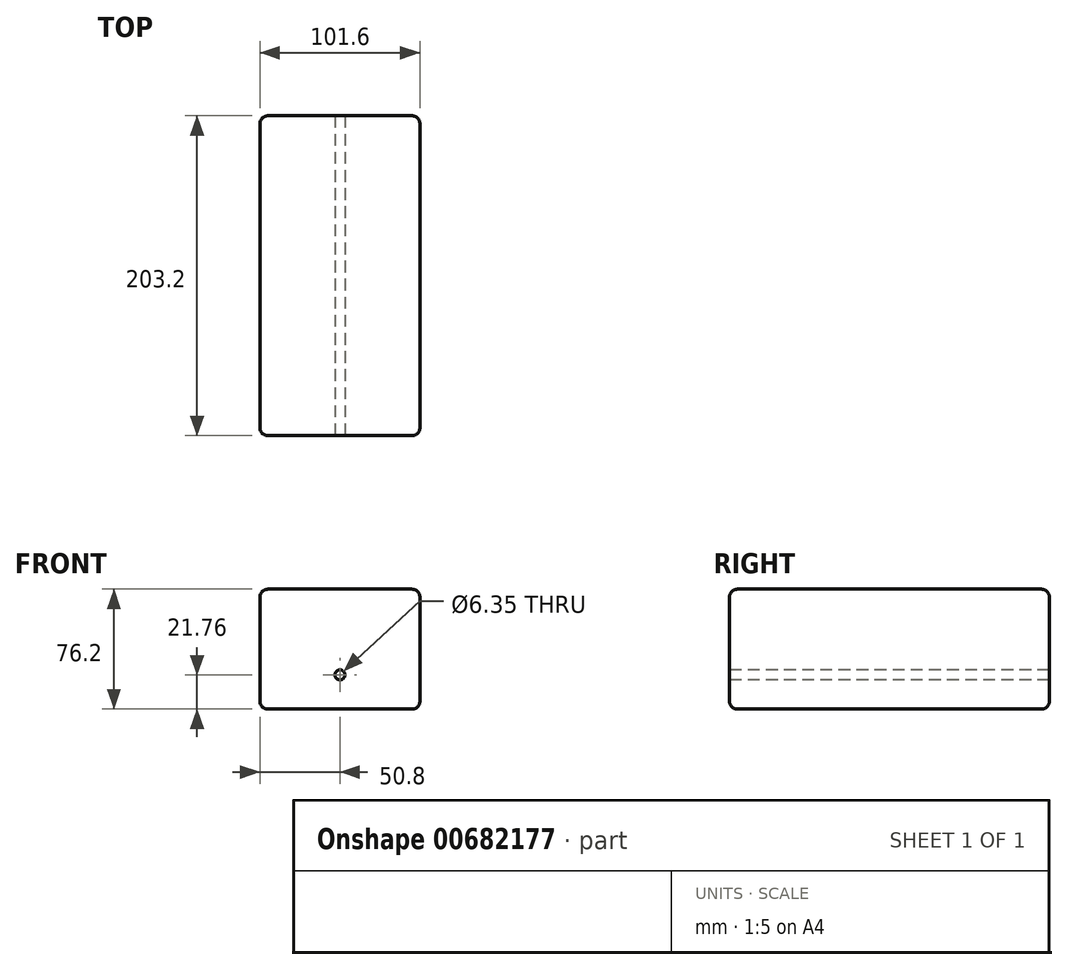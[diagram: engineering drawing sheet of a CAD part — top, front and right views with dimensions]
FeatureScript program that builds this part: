
annotation { "Feature Type Name" : "Feature", "Feature Type Description" : "" }
export const myFeature = defineFeature(function(context is Context, id is Id, definition is map)
    precondition{}
    {
        {
            var Q0;
            Q0=qCreatedBy(makeId("Front.planeOp"),FACE);
            var sketch = newSketch(context, id + "F0", { "sketchPlane" : qUnion([Q0])});
            skLineSegment(sketch, "E0.bottom", {"start": v(-50.8, -38.1) * mm, "end": v(50.8, -38.1) * mm});
            skLineSegment(sketch, "E0.top", {"start": v(-50.8, 38.1) * mm, "end": v(50.8, 38.1) * mm});
            skLineSegment(sketch, "E0.left", {"start": v(-50.8, -38.1) * mm, "end": v(-50.8, 38.1) * mm});
            skLineSegment(sketch, "E0.right", {"start": v(50.8, -38.1) * mm, "end": v(50.8, 38.1) * mm});
            skPoint(sketch, "E0.middle", {"position": v(0, 0) * mm});
            skSolve(sketch);
        }
        {
            var Q0;
            Q0 = qSketchRegion(id + "F0", true);
            extrude(context, id + "F1", {"entities" : qUnion([Q0]), "endBound" : BoundingType.SYMMETRIC, "depth" : 203.2 * mm, "offsetDistance" : 25.4 * mm});
        }
        {
            var Q0;
            Q0=makeQuery(id+"F1.opExtrude","CAP_EDGE",EDGE,{"disambiguationData":[OSD([sQuery(id+"F0.wireOp",EDGE,"E0.top")])],"isStart":false});
            var Q1;
            Q1=makeQuery(id+"F1.opExtrude","SWEPT_EDGE",EDGE,{"disambiguationData":[OSD([sQuery(id+"F0.wireOp",EDGE,"E0.top"),sQuery(id+"F0.wireOp",EDGE,"E0.right")])]});
            var Q2;
            Q2=makeQuery(id+"F1.opExtrude","SWEPT_EDGE",EDGE,{"disambiguationData":[OSD([sQuery(id+"F0.wireOp",EDGE,"E0.top"),sQuery(id+"F0.wireOp",EDGE,"E0.left")])]});
            var Q3;
            Q3=makeQuery(id+"F1.opExtrude","CAP_EDGE",EDGE,{"disambiguationData":[OSD([sQuery(id+"F0.wireOp",EDGE,"E0.left")])],"isStart":false});
            var Q4;
            Q4=makeQuery(id+"F1.opExtrude","CAP_EDGE",EDGE,{"disambiguationData":[OSD([sQuery(id+"F0.wireOp",EDGE,"E0.right")])],"isStart":false});
            var Q5;
            Q5=makeQuery(id+"F1.opExtrude","CAP_FACE",FACE,{"disambiguationData":[OSD([sQuery(id+"F0.wireOp",EDGE,"E0.bottom"),sQuery(id+"F0.wireOp",EDGE,"E0.top"),sQuery(id+"F0.wireOp",EDGE,"E0.left"),sQuery(id+"F0.wireOp",EDGE,"E0.right")])],"isStart":true});
            var Q6;
            Q6=makeQuery(id+"F1.opExtrude","SWEPT_FACE",FACE,{"disambiguationData":[OSD([sQuery(id+"F0.wireOp",EDGE,"E0.right")])]});
            var Q7;
            Q7=makeQuery(id+"F1.opExtrude","SWEPT_EDGE",EDGE,{"disambiguationData":[OSD([sQuery(id+"F0.wireOp",EDGE,"E0.bottom"),sQuery(id+"F0.wireOp",EDGE,"E0.right")])]});
            var Q8;
            Q8=makeQuery(id+"F1.opExtrude","SWEPT_EDGE",EDGE,{"disambiguationData":[OSD([sQuery(id+"F0.wireOp",EDGE,"E0.bottom"),sQuery(id+"F0.wireOp",EDGE,"E0.left")])]});
            fillet(context, id + "F2", {"entities" : qUnion([Q0, Q1, Q2, Q3, Q4, Q5, Q6, Q7, Q8]), "radius" : 5.08 * mm, "tangentPropagation" : true, "allowEdgeOverflow" : false});
        }
        {
            var Q0;
            Q0=makeQuery(id+"FGfTKkmkADLqAxq_1.opShell","OFFSET_EDGE",EDGE,{"disambiguationData":[OSD([sQuery(id+"F0.wireOp",EDGE,"E0.top"),sQuery(id+"F0.wireOp",EDGE,"E0.right")])]});
            var Q1;
            {var subQ0=sQuery(id+"F0.wireOp",EDGE,"E0.top");var subQ1=makeQuery(id+"F1.opExtrude","CAP_EDGE",EDGE,{"disambiguationData":[OSD([subQ0])],"isStart":true});var subQ2=sQuery(id+"F0.wireOp",EDGE,"E0.right");var subQ3=sQuery(id+"F0.wireOp",EDGE,"E0.left");var subQ4=sQuery(id+"F0.wireOp",EDGE,"E0.bottom");Q1=makeQuery(id+"FGfTKkmkADLqAxq_1.opShell","OFFSET_EDGE",EDGE,{"disambiguationData":[OSD([subQ4,subQ0,subQ3,subQ2]),TDD([makeQuery(id+"F2.opFillet","BLEND_EDGE",EDGE,{"blendedFrom":[subQ1,makeQuery(id+"F1.opExtrude","CAP_FACE",FACE,{"disambiguationData":[OSD([subQ4,subQ0,subQ3,subQ2])],"isStart":true})],"blendedInto":[makeQuery(id+"F1.opExtrude","CAP_FACE",FACE,{"disambiguationData":[OSD([subQ4,subQ0,subQ3,subQ2])],"isStart":true})]}),makeQuery(id+"F2.opFillet","BLEND_EDGE",EDGE,{"blendedFrom":[subQ1,makeQuery(id+"F1.opExtrude","SWEPT_FACE",FACE,{"disambiguationData":[OSD([subQ0])]})],"blendedInto":[makeQuery(id+"F1.opExtrude","SWEPT_FACE",FACE,{"disambiguationData":[OSD([subQ0])]})]})])]});}
            var Q2;
            {var subQ0=sQuery(id+"F0.wireOp",EDGE,"E0.left");var subQ1=makeQuery(id+"F1.opExtrude","CAP_EDGE",EDGE,{"disambiguationData":[OSD([subQ0])],"isStart":true});var subQ2=sQuery(id+"F0.wireOp",EDGE,"E0.right");var subQ3=sQuery(id+"F0.wireOp",EDGE,"E0.top");var subQ4=sQuery(id+"F0.wireOp",EDGE,"E0.bottom");Q2=makeQuery(id+"FGfTKkmkADLqAxq_1.opShell","OFFSET_EDGE",EDGE,{"disambiguationData":[OSD([subQ4,subQ3,subQ0,subQ2]),TDD([makeQuery(id+"F2.opFillet","BLEND_EDGE",EDGE,{"blendedFrom":[subQ1,makeQuery(id+"F1.opExtrude","CAP_FACE",FACE,{"disambiguationData":[OSD([subQ4,subQ3,subQ0,subQ2])],"isStart":true})],"blendedInto":[makeQuery(id+"F1.opExtrude","CAP_FACE",FACE,{"disambiguationData":[OSD([subQ4,subQ3,subQ0,subQ2])],"isStart":true})]}),makeQuery(id+"F2.opFillet","BLEND_EDGE",EDGE,{"blendedFrom":[subQ1,makeQuery(id+"F1.opExtrude","SWEPT_FACE",FACE,{"disambiguationData":[OSD([subQ0])]})],"blendedInto":[makeQuery(id+"F1.opExtrude","SWEPT_FACE",FACE,{"disambiguationData":[OSD([subQ0])]})]})])]});}
            var Q3;
            {var subQ0=sQuery(id+"F0.wireOp",EDGE,"E0.right");var subQ1=makeQuery(id+"F1.opExtrude","CAP_EDGE",EDGE,{"disambiguationData":[OSD([subQ0])],"isStart":true});var subQ2=sQuery(id+"F0.wireOp",EDGE,"E0.left");var subQ3=sQuery(id+"F0.wireOp",EDGE,"E0.top");var subQ4=sQuery(id+"F0.wireOp",EDGE,"E0.bottom");Q3=makeQuery(id+"FGfTKkmkADLqAxq_1.opShell","OFFSET_EDGE",EDGE,{"disambiguationData":[OSD([subQ4,subQ3,subQ2,subQ0]),TDD([makeQuery(id+"F2.opFillet","BLEND_EDGE",EDGE,{"blendedFrom":[subQ1,makeQuery(id+"F1.opExtrude","CAP_FACE",FACE,{"disambiguationData":[OSD([subQ4,subQ3,subQ2,subQ0])],"isStart":true})],"blendedInto":[makeQuery(id+"F1.opExtrude","CAP_FACE",FACE,{"disambiguationData":[OSD([subQ4,subQ3,subQ2,subQ0])],"isStart":true})]}),makeQuery(id+"F2.opFillet","BLEND_EDGE",EDGE,{"blendedFrom":[subQ1,makeQuery(id+"F1.opExtrude","SWEPT_FACE",FACE,{"disambiguationData":[OSD([subQ0])]})],"blendedInto":[makeQuery(id+"F1.opExtrude","SWEPT_FACE",FACE,{"disambiguationData":[OSD([subQ0])]})]})])]});}
            var Q4;
            Q4=makeQuery(id+"FGfTKkmkADLqAxq_1.opShell","OFFSET_EDGE",EDGE,{"disambiguationData":[OSD([sQuery(id+"F0.wireOp",EDGE,"E0.top"),sQuery(id+"F0.wireOp",EDGE,"E0.left")])]});
            var Q5;
            {var subQ0=sQuery(id+"F0.wireOp",EDGE,"E0.right");var subQ1=sQuery(id+"F0.wireOp",EDGE,"E0.left");var subQ2=sQuery(id+"F0.wireOp",EDGE,"E0.top");var subQ3=sQuery(id+"F0.wireOp",EDGE,"E0.bottom");var subQ4=makeQuery(id+"F1.opExtrude","CAP_EDGE",EDGE,{"disambiguationData":[OSD([subQ3])],"isStart":true});Q5=makeQuery(id+"FGfTKkmkADLqAxq_1.opShell","OFFSET_EDGE",EDGE,{"disambiguationData":[OSD([subQ3,subQ2,subQ1,subQ0]),TDD([makeQuery(id+"F2.opFillet","BLEND_EDGE",EDGE,{"blendedFrom":[subQ4,makeQuery(id+"F1.opExtrude","SWEPT_FACE",FACE,{"disambiguationData":[OSD([subQ3])]})],"blendedInto":[makeQuery(id+"F1.opExtrude","SWEPT_FACE",FACE,{"disambiguationData":[OSD([subQ3])]})]}),makeQuery(id+"F2.opFillet","BLEND_EDGE",EDGE,{"blendedFrom":[subQ4,makeQuery(id+"F1.opExtrude","CAP_FACE",FACE,{"disambiguationData":[OSD([subQ3,subQ2,subQ1,subQ0])],"isStart":true})],"blendedInto":[makeQuery(id+"F1.opExtrude","CAP_FACE",FACE,{"disambiguationData":[OSD([subQ3,subQ2,subQ1,subQ0])],"isStart":true})]})])]});}
            var Q6;
            Q6=makeQuery(id+"FGfTKkmkADLqAxq_1.opShell","OFFSET_EDGE",EDGE,{"disambiguationData":[OSD([sQuery(id+"F0.wireOp",EDGE,"E0.bottom"),sQuery(id+"F0.wireOp",EDGE,"E0.left")])]});
            var Q7;
            Q7=makeQuery(id+"FGfTKkmkADLqAxq_1.opShell","OFFSET_EDGE",EDGE,{"disambiguationData":[OSD([sQuery(id+"F0.wireOp",EDGE,"E0.bottom")])]});
            var Q8;
            {var subQ0=sQuery(id+"F0.wireOp",EDGE,"E0.left");var subQ1=makeQuery(id+"F1.opExtrude","CAP_EDGE",EDGE,{"disambiguationData":[OSD([subQ0])],"isStart":false});var subQ2=sQuery(id+"F0.wireOp",EDGE,"E0.right");var subQ3=sQuery(id+"F0.wireOp",EDGE,"E0.top");var subQ4=sQuery(id+"F0.wireOp",EDGE,"E0.bottom");Q8=makeQuery(id+"FGfTKkmkADLqAxq_1.opShell","OFFSET_EDGE",EDGE,{"disambiguationData":[OSD([subQ4,subQ3,subQ0,subQ2]),TDD([makeQuery(id+"F2.opFillet","BLEND_EDGE",EDGE,{"blendedFrom":[subQ1,makeQuery(id+"F1.opExtrude","CAP_FACE",FACE,{"disambiguationData":[OSD([subQ4,subQ3,subQ0,subQ2])],"isStart":false})],"blendedInto":[makeQuery(id+"F1.opExtrude","CAP_FACE",FACE,{"disambiguationData":[OSD([subQ4,subQ3,subQ0,subQ2])],"isStart":false})]}),makeQuery(id+"F2.opFillet","BLEND_EDGE",EDGE,{"blendedFrom":[subQ1,makeQuery(id+"F1.opExtrude","SWEPT_FACE",FACE,{"disambiguationData":[OSD([subQ0])]})],"blendedInto":[makeQuery(id+"F1.opExtrude","SWEPT_FACE",FACE,{"disambiguationData":[OSD([subQ0])]})]})])]});}
            var Q9;
            {var subQ0=sQuery(id+"F0.wireOp",EDGE,"E0.top");var subQ1=makeQuery(id+"F1.opExtrude","CAP_EDGE",EDGE,{"disambiguationData":[OSD([subQ0])],"isStart":false});var subQ2=sQuery(id+"F0.wireOp",EDGE,"E0.right");var subQ3=sQuery(id+"F0.wireOp",EDGE,"E0.left");var subQ4=sQuery(id+"F0.wireOp",EDGE,"E0.bottom");Q9=makeQuery(id+"FGfTKkmkADLqAxq_1.opShell","OFFSET_EDGE",EDGE,{"disambiguationData":[OSD([subQ4,subQ0,subQ3,subQ2]),TDD([makeQuery(id+"F2.opFillet","BLEND_EDGE",EDGE,{"blendedFrom":[subQ1,makeQuery(id+"F1.opExtrude","CAP_FACE",FACE,{"disambiguationData":[OSD([subQ4,subQ0,subQ3,subQ2])],"isStart":false})],"blendedInto":[makeQuery(id+"F1.opExtrude","CAP_FACE",FACE,{"disambiguationData":[OSD([subQ4,subQ0,subQ3,subQ2])],"isStart":false})]}),makeQuery(id+"F2.opFillet","BLEND_EDGE",EDGE,{"blendedFrom":[subQ1,makeQuery(id+"F1.opExtrude","SWEPT_FACE",FACE,{"disambiguationData":[OSD([subQ0])]})],"blendedInto":[makeQuery(id+"F1.opExtrude","SWEPT_FACE",FACE,{"disambiguationData":[OSD([subQ0])]})]})])]});}
            var Q10;
            Q10=makeQuery(id+"FGfTKkmkADLqAxq_1.opShell","OFFSET_EDGE",EDGE,{"disambiguationData":[OSD([sQuery(id+"F0.wireOp",EDGE,"E0.bottom"),sQuery(id+"F0.wireOp",EDGE,"E0.right")])]});
            var Q11;
            {var subQ0=sQuery(id+"F0.wireOp",EDGE,"E0.right");var subQ1=makeQuery(id+"F1.opExtrude","CAP_EDGE",EDGE,{"disambiguationData":[OSD([subQ0])],"isStart":false});var subQ2=sQuery(id+"F0.wireOp",EDGE,"E0.left");var subQ3=sQuery(id+"F0.wireOp",EDGE,"E0.top");var subQ4=sQuery(id+"F0.wireOp",EDGE,"E0.bottom");Q11=makeQuery(id+"FGfTKkmkADLqAxq_1.opShell","OFFSET_EDGE",EDGE,{"disambiguationData":[OSD([subQ4,subQ3,subQ2,subQ0]),TDD([makeQuery(id+"F2.opFillet","BLEND_EDGE",EDGE,{"blendedFrom":[subQ1,makeQuery(id+"F1.opExtrude","CAP_FACE",FACE,{"disambiguationData":[OSD([subQ4,subQ3,subQ2,subQ0])],"isStart":false})],"blendedInto":[makeQuery(id+"F1.opExtrude","CAP_FACE",FACE,{"disambiguationData":[OSD([subQ4,subQ3,subQ2,subQ0])],"isStart":false})]}),makeQuery(id+"F2.opFillet","BLEND_EDGE",EDGE,{"blendedFrom":[subQ1,makeQuery(id+"F1.opExtrude","SWEPT_FACE",FACE,{"disambiguationData":[OSD([subQ0])]})],"blendedInto":[makeQuery(id+"F1.opExtrude","SWEPT_FACE",FACE,{"disambiguationData":[OSD([subQ0])]})]})])]});}
            var Q12;
            {var subQ0=sQuery(id+"F0.wireOp",EDGE,"E0.right");Q12=makeQuery(id+"F2.opFillet","BLEND_EDGE",EDGE,{"blendedFrom":[makeQuery(id+"F1.opExtrude","CAP_EDGE",EDGE,{"disambiguationData":[OSD([subQ0])],"isStart":false}),makeQuery(id+"F1.opExtrude","CAP_FACE",FACE,{"disambiguationData":[OSD([sQuery(id+"F0.wireOp",EDGE,"E0.bottom"),sQuery(id+"F0.wireOp",EDGE,"E0.top"),sQuery(id+"F0.wireOp",EDGE,"E0.left"),subQ0])],"isStart":false})],"blendedInto":[makeQuery(id+"F1.opExtrude","CAP_FACE",FACE,{"disambiguationData":[OSD([sQuery(id+"F0.wireOp",EDGE,"E0.bottom"),sQuery(id+"F0.wireOp",EDGE,"E0.top"),sQuery(id+"F0.wireOp",EDGE,"E0.left"),subQ0])],"isStart":false})]});}
            var Q13;
            {var subQ0=sQuery(id+"F0.wireOp",EDGE,"E0.bottom");Q13=makeQuery(id+"F2.opFillet","BLEND_EDGE",EDGE,{"blendedFrom":[makeQuery(id+"F1.opExtrude","SWEPT_EDGE",EDGE,{"disambiguationData":[OSD([subQ0,sQuery(id+"F0.wireOp",EDGE,"E0.right")])]}),makeQuery(id+"F1.opExtrude","SWEPT_FACE",FACE,{"disambiguationData":[OSD([subQ0])]})],"blendedInto":[makeQuery(id+"F1.opExtrude","SWEPT_FACE",FACE,{"disambiguationData":[OSD([subQ0])]})]});}
            var Q14;
            Q14=makeQuery(id+"F1.opExtrude","CAP_EDGE",EDGE,{"disambiguationData":[OSD([sQuery(id+"F0.wireOp",EDGE,"E0.bottom")])],"isStart":false});
            fillet(context, id + "F3", {"entities" : qUnion([Q0, Q1, Q2, Q3, Q4, Q5, Q6, Q7, Q8, Q9, Q10, Q11, Q12, Q13, Q14]), "radius" : 5.08 * mm, "tangentPropagation" : true, "allowEdgeOverflow" : false});
        }
        {
            var Q0;
            Q0=makeQuery(id+"F1.opExtrude","CAP_FACE",FACE,{"disambiguationData":[OSD([sQuery(id+"F0.wireOp",EDGE,"E0.bottom"),sQuery(id+"F0.wireOp",EDGE,"E0.top"),sQuery(id+"F0.wireOp",EDGE,"E0.left"),sQuery(id+"F0.wireOp",EDGE,"E0.right")])],"isStart":false});
            var sketch = newSketch(context, id + "F4", { "sketchPlane" : qUnion([Q0])});
            skCircle(sketch, "E1", {"center": v(0, -16.34) * mm, "radius": 3.18 * mm});
            skSolve(sketch);
        }
        {
            var Q0;
            Q0=makeQuery(id+"F4.imprint","IMPRINT",FACE,{"disambiguationData":[TD([[makeQuery(id+"F4.imprint","IMPRINT",EDGE,{"derivedFrom":sQuery(id+"F4.wireOp",EDGE,"E1")}),1.0]])]});
            var Q1;
            Q1=makeQuery(id+"F1.opExtrude","CAP_FACE",FACE,{"disambiguationData":[OSD([sQuery(id+"F0.wireOp",EDGE,"E0.bottom"),sQuery(id+"F0.wireOp",EDGE,"E0.top"),sQuery(id+"F0.wireOp",EDGE,"E0.left"),sQuery(id+"F0.wireOp",EDGE,"E0.right")])],"isStart":true});
            extrude(context, id + "F5", {"entities" : qUnion([Q0]), "operationType" : NewBodyOperationType.REMOVE, "endBound" : BoundingType.UP_TO_SURFACE, "oppositeDirection" : true, "depth" : 63.5 * mm, "endBoundEntityFace" : qUnion([Q1]), "offsetDistance" : 25.4 * mm});
        }
        {
            var Q0;
            Q0=makeQuery(id+"F1.opExtrude","CAP_FACE",FACE,{"disambiguationData":[OSD([sQuery(id+"F0.wireOp",EDGE,"E0.bottom"),sQuery(id+"F0.wireOp",EDGE,"E0.top"),sQuery(id+"F0.wireOp",EDGE,"E0.left"),sQuery(id+"F0.wireOp",EDGE,"E0.right")])],"isStart":false});
            var sketch = newSketch(context, id + "F6", { "sketchPlane" : qUnion([Q0])});
            skCircle(sketch, "E2", {"center": v(0, -16.34) * mm, "radius": 3.17 * mm});
            skSolve(sketch);
        }
        {
            var Q0;
            Q0 = qSketchRegion(id + "F6", true);
            var Q1;
            Q1=sQuery(id+"F6.wireOp",EDGE,"E2");
            extrude(context, id + "F7", {"entities" : qUnion([Q0]), "bodyType" : ToolBodyType.SURFACE, "surfaceEntities" : qUnion([Q1]), "depth" : 127 * mm, "offsetDistance" : 25.4 * mm});
        }
        {
            var Q0;
            Q0=makeQuery(id+"F1.opExtrude","CAP_FACE",FACE,{"disambiguationData":[OSD([sQuery(id+"F0.wireOp",EDGE,"E0.bottom"),sQuery(id+"F0.wireOp",EDGE,"E0.top"),sQuery(id+"F0.wireOp",EDGE,"E0.left"),sQuery(id+"F0.wireOp",EDGE,"E0.right")])],"isStart":true});
            var sketch = newSketch(context, id + "F8", { "sketchPlane" : qUnion([Q0])});
            skCircle(sketch, "E3", {"center": v(0, -16.34) * mm, "radius": 3.18 * mm});
            skSolve(sketch);
        }
        {
            var Q0;
            Q0 = qSketchRegion(id + "F8", true);
            var Q1;
            Q1 = qConstructionFilter(qBodyType(qCreatedBy(id + "F8" ,EDGE), BodyType.WIRE), ConstructionObject.NO);
            extrude(context, id + "F9", {"entities" : qUnion([Q0]), "bodyType" : ToolBodyType.SURFACE, "operationType" : NewBodyOperationType.ADD, "surfaceEntities" : qUnion([Q1]), "depth" : 127 * mm, "hasOffset" : true, "offsetDistance" : 127 * mm});
        }
    });
